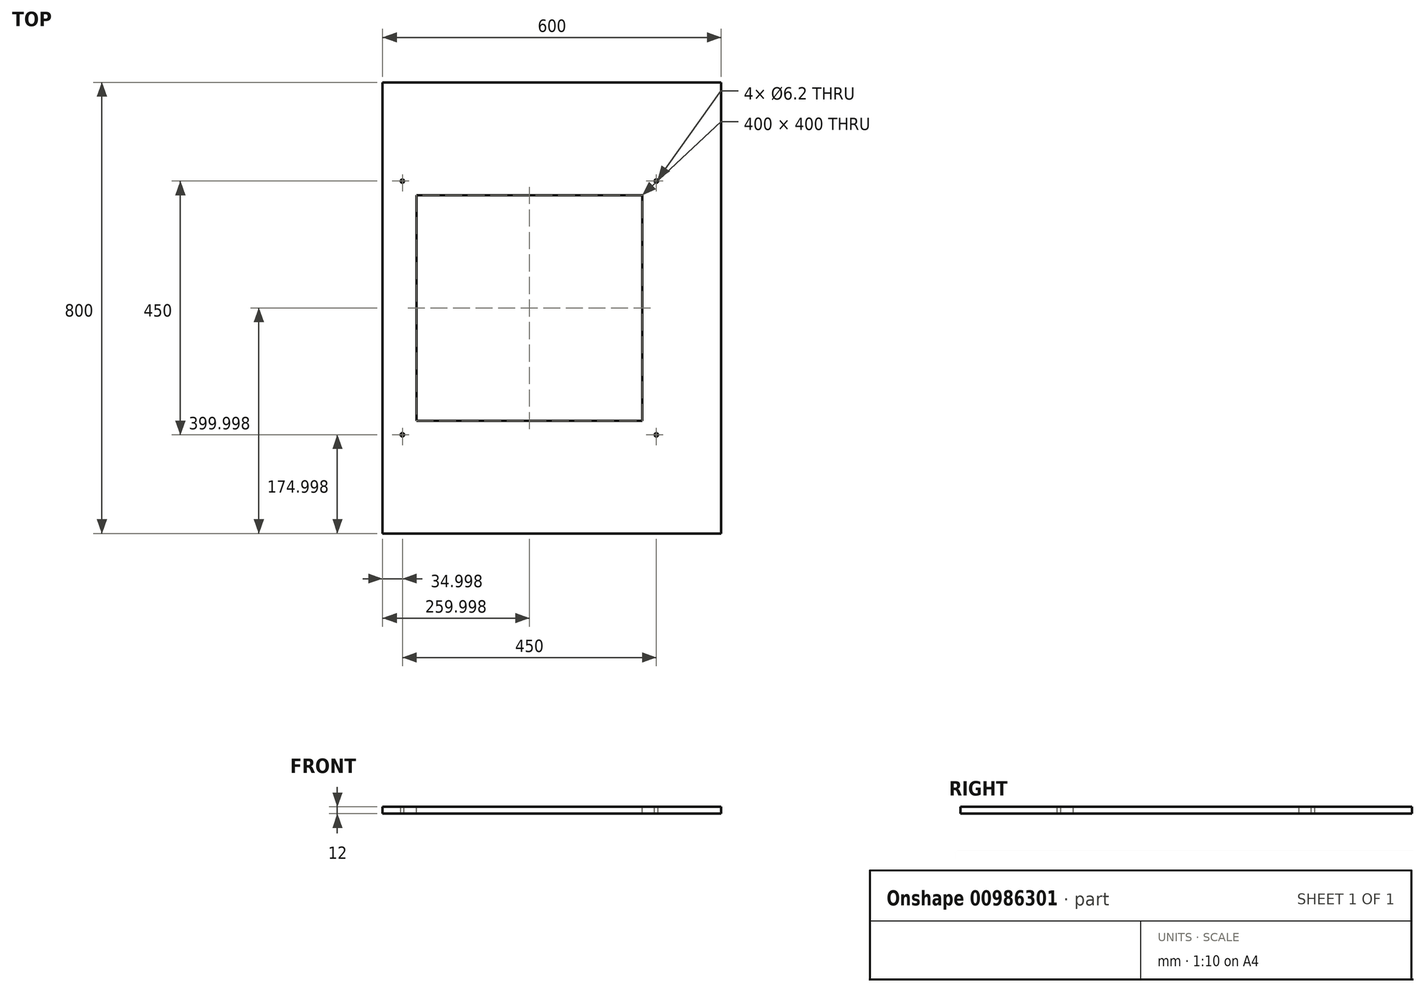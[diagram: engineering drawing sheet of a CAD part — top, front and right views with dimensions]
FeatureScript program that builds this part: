
annotation { "Feature Type Name" : "Feature", "Feature Type Description" : "" }
export const myFeature = defineFeature(function(context is Context, id is Id, definition is map)
    precondition{}
    {
        {
            var Q0;
            Q0=qCreatedBy(makeId("Top.planeOp"),FACE);
            var sketch = newSketch(context, id + "F0", { "sketchPlane" : qUnion([Q0])});
            skLineSegment(sketch, "E0.bottom", {"start": v(-226.68, 125.06) * mm, "end": v(373.32, 125.06) * mm});
            skLineSegment(sketch, "E0.top", {"start": v(-226.68, -674.94) * mm, "end": v(373.32, -674.94) * mm});
            skLineSegment(sketch, "E0.left", {"start": v(-226.68, 125.06) * mm, "end": v(-226.68, -674.94) * mm});
            skLineSegment(sketch, "E0.right", {"start": v(373.32, 125.06) * mm, "end": v(373.32, -674.94) * mm});
            skSolve(sketch);
        }
        {
            var Q0;
            Q0 = qSketchRegion(id + "F0", true);
            extrude(context, id + "F1", {"entities" : qUnion([Q0]), "depth" : 12 * mm, "offsetDistance" : 25 * mm});
        }
        {
            var Q0;
            Q0=makeQuery(id+"F1.opExtrude","CAP_FACE",FACE,{"disambiguationData":[OSD([sQuery(id+"F0.wireOp",EDGE,"E0.bottom"),sQuery(id+"F0.wireOp",EDGE,"E0.top"),sQuery(id+"F0.wireOp",EDGE,"E0.left"),sQuery(id+"F0.wireOp",EDGE,"E0.right")])],"isStart":false});
            var sketch = newSketch(context, id + "F2", { "sketchPlane" : qUnion([Q0])});
            skLineSegment(sketch, "E1.bottom", {"start": v(-166.68, -74.94) * mm, "end": v(233.32, -74.94) * mm});
            skLineSegment(sketch, "E1.top", {"start": v(-166.68, -474.94) * mm, "end": v(233.32, -474.94) * mm});
            skLineSegment(sketch, "E1.left", {"start": v(-166.68, -74.94) * mm, "end": v(-166.68, -474.94) * mm});
            skLineSegment(sketch, "E1.right", {"start": v(233.32, -74.94) * mm, "end": v(233.32, -474.94) * mm});
            skSolve(sketch);
        }
        {
            var Q0;
            Q0 = qSketchRegion(id + "F2", true);
            extrude(context, id + "F3", {"entities" : qUnion([Q0]), "operationType" : NewBodyOperationType.REMOVE, "oppositeDirection" : true, "depth" : 15 * mm, "offsetDistance" : 25 * mm});
        }
        {
            var Q0;
            Q0=makeQuery(id+"F1.opExtrude","CAP_FACE",FACE,{"disambiguationData":[OSD([sQuery(id+"F0.wireOp",EDGE,"E0.bottom"),sQuery(id+"F0.wireOp",EDGE,"E0.top"),sQuery(id+"F0.wireOp",EDGE,"E0.left"),sQuery(id+"F0.wireOp",EDGE,"E0.right")])],"isStart":false});
            var sketch = newSketch(context, id + "F4", { "sketchPlane" : qUnion([Q0])});
            skCircle(sketch, "E2", {"center": v(-191.68, -49.94) * mm, "radius": 6 * mm});
            skCircle(sketch, "E3.0.1.0", {"center": v(-191.68, -499.94) * mm, "radius": 6 * mm});
            skCircle(sketch, "E3.1.0.0", {"center": v(258.32, -49.94) * mm, "radius": 6 * mm});
            skCircle(sketch, "E3.1.1.0", {"center": v(258.32, -499.94) * mm, "radius": 6 * mm});
            skLineSegment(sketch, "E3.direction1", {"start": v(-191.68, -49.94) * mm, "end": v(258.32, -49.94) * mm, "construction": true});
            skLineSegment(sketch, "E3.direction2", {"start": v(-191.68, -49.94) * mm, "end": v(-191.68, -499.94) * mm, "construction": true});
            skSolve(sketch);
        }
        {
            var Q0;
            Q0=makeQuery(id+"F4.imprint","IMPRINT",FACE,{"disambiguationData":[TD([[makeQuery(id+"F4.imprint","IMPRINT",EDGE,{"derivedFrom":sQuery(id+"F4.wireOp",EDGE,"E2")}),-1.0]])]});
            var sketch = newSketch(context, id + "F5", { "sketchPlane" : qUnion([Q0])});
            skCircle(sketch, "E4", {"center": v(-191.68, -49.94) * mm, "radius": 3.1 * mm});
            skCircle(sketch, "E5.0.1.0", {"center": v(-191.68, -499.94) * mm, "radius": 3.1 * mm});
            skCircle(sketch, "E5.1.0.0", {"center": v(258.32, -49.94) * mm, "radius": 3.1 * mm});
            skCircle(sketch, "E5.1.1.0", {"center": v(258.32, -499.94) * mm, "radius": 3.1 * mm});
            skLineSegment(sketch, "E5.direction1", {"start": v(-191.68, -49.94) * mm, "end": v(258.32, -49.94) * mm, "construction": true});
            skLineSegment(sketch, "E5.direction2", {"start": v(-191.68, -49.94) * mm, "end": v(-191.68, -499.94) * mm, "construction": true});
            skSolve(sketch);
        }
        {
            var Q0;
            Q0 = qSketchRegion(id + "F5", true);
            extrude(context, id + "F6", {"entities" : qUnion([Q0]), "operationType" : NewBodyOperationType.REMOVE, "oppositeDirection" : true, "depth" : 50 * mm, "offsetDistance" : 25 * mm});
        }
    });
